# Revit family: Building-ContenitoriParete-GEWISS-40CDK-CENTRALINI_IP65_1X
name_source: partatom
category: Apparecchi elettrici
revit_build: Autodesk Revit 2016 (Build: 20161004_0715(x64)
units: mm (PartAtom-declared; Revit-internal decimal feet)

## family parameters
Condiviso = No
Host = Superficie
Mantenere orientamento annotazione = Sì
Numero OmniClass = 23.80.30.11.17
Punto di calcolo locali = Sì
Quota connettore circolare = Usa diametro
Taglio con vuoti quando caricato = No
Tipo di parte = Normale
Titolo OmniClass = Distribution Boards and Control Panels

## types (4) — shared parameters
Catalogo = BUILDING
Catalogo Serie = 40 CDK
Classe isolamento = II (secondo Norma IEC 61140)
Codice Electrocod = 0321
Colore = Grigio RAL 7035
Corrente nominale: = 125A
Diametro_tubazione = 30 mm  [stored 0.0984252 ft]
Dimensione modulo = 18 mm  [stored 0.0590551 ft]
Glow Wire Test = 650°C
Grado di protezione = IP65
H_finestratura = 45 mm  [stored 0.147638 ft]
H_quadro = 285 mm  [stored 0.935039 ft]
IDF = 49e0ccd0-3d3c-41b4-957d-47fcc2f698ee
IDT = 09bc94ce-5498-4c76-bae9-7f0a749fa703
L_finestratura = 324 mm  [stored 1.06299 ft]
L_quadro = 410 mm  [stored 1.34514 ft]
N.M. = 18
Norma di riferimento = EN 60670-1 (CEI 23-48) IEC60670-24 CEI 23-49
Normativa = EN 60670-1 (CEI 23-48) IEC60670-24 CEI 23-49
Produttore = GEWISS S.p.A.
Prondita_quadro = 140 mm  [stored 0.459318 ft]
Prospetto di default = 1219 mm
Resistenza agli urti = IK09
SEO = Centralino
Scheda Tecnica = https://www.gewiss.com
Sportello = Sportello_trasparente
Spostamento_Y = 560 mm
Temperatura di impiego = -25 +60 °C
Tensione di isolamento: = 1000 V secondo EN 62208 sia in ac che in dc
Tensione nominale = 400V
Tensione nominale di isolamento (Ui) = 1000 V
Termopressione con biglia = 70 °C
Tipo Materiale = Halogen free secondo norma EN 60754-2
URL = https://www.gewiss.com
Versione file RFA = 18.0
fase1 = 0 VA
h_sportello = 225 mm  [stored 0.738189 ft]
s = 262 mm
voltaggio_quadro = 0 V

## per-type parameters (varying)
| type | Accessori per ripristino isolamento | Codice EAN | Colore porta | Descrizione | Dim. esterne BxHxP (mm) | Max.morsettiere installabili | Modello | N. mod. EN 50022 | N. mod. EN 50022: | Potenza dissipabile (W) | Tensione di isolamento |
| GW40101 - CENTRALINO PARETE 4M.IP65 |  | 8011564061477 |  | CENTRALINO PARETE 4M.IP65 | 143x210x100 |  | GW40101 | 4 | 4 | 13 | 1000V |
| GW40106 - CENTRALINO PARETE 18M.IP65 | Tappi coprivite (GW44623) o staffe di fissaggio in resina (GW44621) | 8011564061576 | Trasparente fume' | CENTRALINO PARETE 18M.IP65 | 410x285x140 | 1 x 18 moduli | GW40106 | 18 | 18 | 38 |  |
| GW40102 - CENTRALINO PARETE 8M.IP65 | Tappi coprivite (GW44623) o staffe di fissaggio in resina (GW44621) | 8011564061514 | Trasparente fume' | CENTRALINO PARETE 8M.IP65 | 215x210x100 | 1 x 8 moduli | GW40102 | 8 | 8 | 16 |  |
| GW40103 - CENTRALINO PARETE 12M.IP65 | Tappi coprivite (GW44623) o staffe di fissaggio in resina (GW44621) | 8011564061545 | Trasparente fume' | CENTRALINO PARETE 12M.IP65 | 298x260x140 | 1 x 12 moduli | GW40103 | 12 | 12 | 26 |  |

note: [stored X ft] marks values corroborated as IEEE doubles in the binary element streams (Revit-internal decimal feet)

## geometry (parser evidence)
native form markers: Sweep x1
no freeform markers — native parametric forms only
